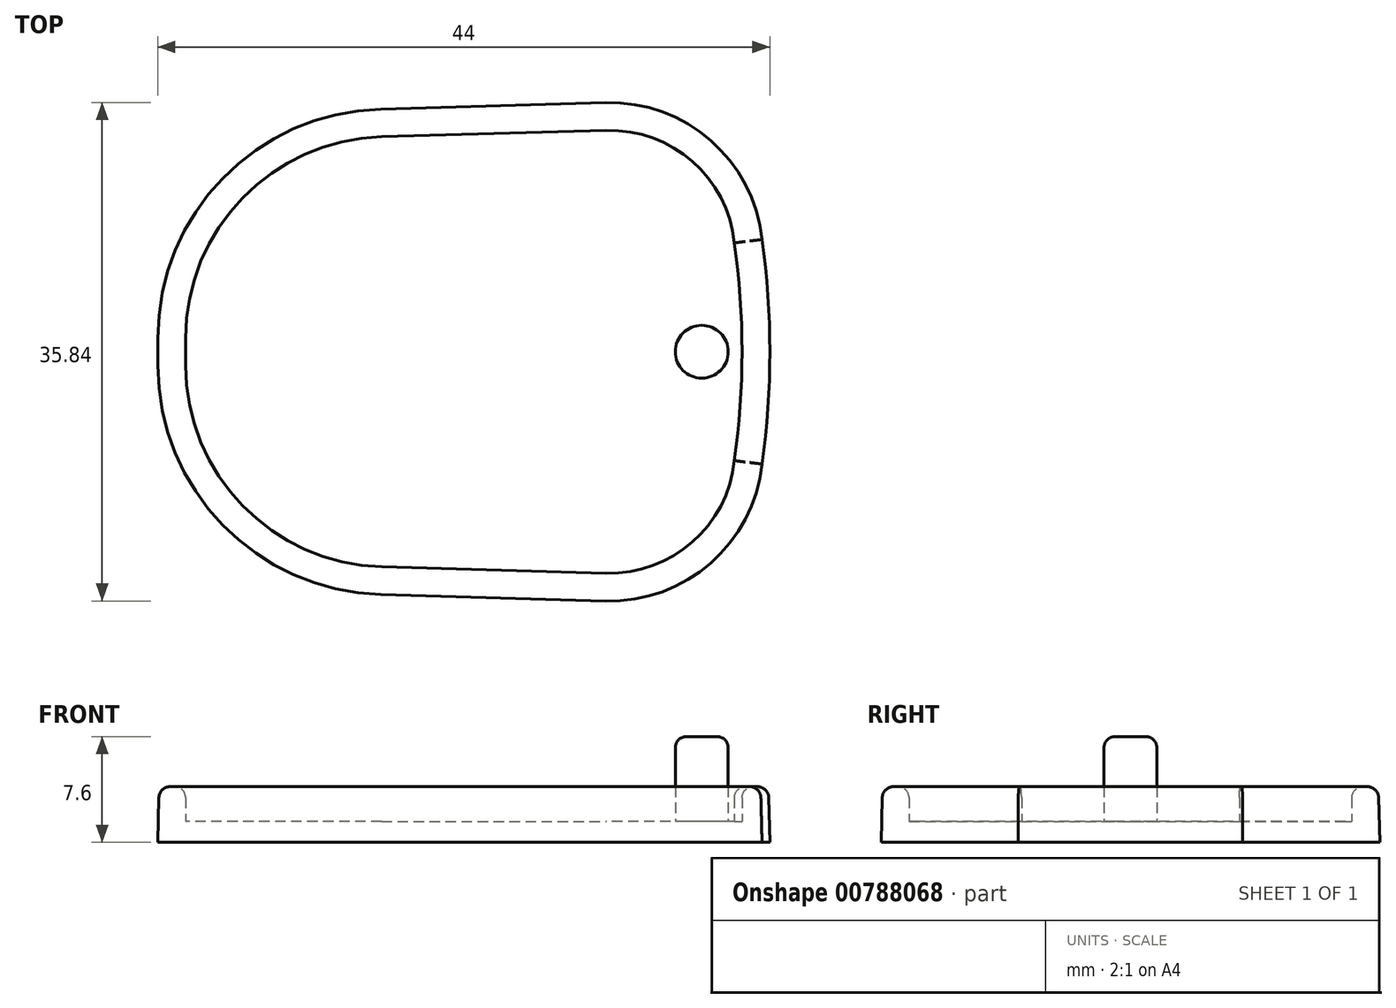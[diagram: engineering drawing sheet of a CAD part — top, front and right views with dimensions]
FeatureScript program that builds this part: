
annotation { "Feature Type Name" : "Feature", "Feature Type Description" : "" }
export const myFeature = defineFeature(function(context is Context, id is Id, definition is map)
    precondition{}
    {
        {
            var Q0;
            Q0=qCreatedBy(makeId("Top.planeOp"),FACE);
            var sketch = newSketch(context, id + "F0", { "sketchPlane" : qUnion([Q0])});
            skLineSegment(sketch, "E0", {"start": v(-22, 17) * mm, "end": v(22, 18.25) * mm, "construction": true});
            skLineSegment(sketch, "E1", {"start": v(22, 18.25) * mm, "end": v(22, -18.25) * mm, "construction": true});
            skLineSegment(sketch, "E2", {"start": v(22, -18.25) * mm, "end": v(-22, -17) * mm, "construction": true});
            skLineSegment(sketch, "E3", {"start": v(-22, -17) * mm, "end": v(-22, 17) * mm, "construction": true});
            skPoint(sketch, "E4", {"position": v(-22, 0) * mm});
            skPoint(sketch, "E5", {"position": v(22, 0) * mm});
            skPoint(sketch, "E6", {"position": v(0, 17.63) * mm});
            skArc(sketch, "E7", {"start": v(-5.97, 17.46) * mm, "mid": v(-17.33, 12.46) * mm, "end": v(-22, 0.96) * mm});
            skLineSegment(sketch, "E8", {"start": v(-22, 0) * mm, "end": v(-22, 0.96) * mm});
            skArc(sketch, "E9", {"start": v(22, 0) * mm, "mid": v(21.86, 4.05) * mm, "end": v(21.44, 8.07) * mm});
            skArc(sketch, "E10", {"start": v(21.44, 8.07) * mm, "mid": v(17.74, 15.2) * mm, "end": v(10.18, 17.91) * mm});
            skLineSegment(sketch, "E11", {"start": v(-36, 0) * mm, "end": v(21.44, 8.07) * mm, "construction": true});
            skLineSegment(sketch, "E12", {"start": v(-12.73, 0) * mm, "end": v(12.59, 0) * mm, "construction": true});
            skLineSegment(sketch, "E13.MirrorCS", {"start": v(-22, 0) * mm, "end": v(-22, -0.96) * mm});
            skArc(sketch, "E14.MirrorCS", {"start": v(-5.97, -17.46) * mm, "mid": v(-17.33, -12.46) * mm, "end": v(-22, -0.96) * mm});
            skPoint(sketch, "E15.MirrorP", {"position": v(0, -17.63) * mm});
            skArc(sketch, "E16.MirrorCS", {"start": v(21.44, -8.07) * mm, "mid": v(17.74, -15.2) * mm, "end": v(10.18, -17.91) * mm});
            skArc(sketch, "E17.MirrorCS", {"start": v(22, 0) * mm, "mid": v(21.86, -4.05) * mm, "end": v(21.44, -8.07) * mm});
            skLineSegment(sketch, "E18", {"start": v(-5.97, 17.46) * mm, "end": v(10.18, 17.91) * mm});
            skLineSegment(sketch, "E19", {"start": v(-5.97, -17.46) * mm, "end": v(10.18, -17.91) * mm});
            skCircle(sketch, "E20", {"center": v(17.1, 0) * mm, "radius": 1.9 * mm});
            skLineSegment(sketch, "E21.0", {"start": v(-5.91, 15.46) * mm, "end": v(10.24, 15.92) * mm});
            skArc(sketch, "E21.1", {"start": v(19.45, 7.83) * mm, "mid": v(16.43, 13.68) * mm, "end": v(10.24, 15.92) * mm});
            skArc(sketch, "E21.2", {"start": v(-5.91, 15.46) * mm, "mid": v(-15.9, 11.07) * mm, "end": v(-20, 0.96) * mm});
            skArc(sketch, "E21.3", {"start": v(20, 0) * mm, "mid": v(19.86, 3.92) * mm, "end": v(19.45, 7.83) * mm});
            skArc(sketch, "E21.4", {"start": v(20, 0) * mm, "mid": v(19.86, -3.92) * mm, "end": v(19.45, -7.83) * mm});
            skArc(sketch, "E21.5", {"start": v(19.45, -7.83) * mm, "mid": v(16.43, -13.68) * mm, "end": v(10.24, -15.92) * mm});
            skLineSegment(sketch, "E21.6", {"start": v(-20, 0) * mm, "end": v(-20, 0.96) * mm});
            skLineSegment(sketch, "E21.7", {"start": v(-20, 0) * mm, "end": v(-20, -0.96) * mm});
            skArc(sketch, "E21.8", {"start": v(-5.91, -15.46) * mm, "mid": v(-15.9, -11.07) * mm, "end": v(-20, -0.96) * mm});
            skLineSegment(sketch, "E21.9", {"start": v(-5.91, -15.46) * mm, "end": v(10.24, -15.92) * mm});
            skSolve(sketch);
        }
        {
            var Q0;
            Q0=makeQuery(id+"F0.imprint","IMPRINT",FACE,{"disambiguationData":[TD([[makeQuery(id+"F0.imprint","IMPRINT",EDGE,{"derivedFrom":sQuery(id+"F0.wireOp",EDGE,"E7")}),1.0]])]});
            extrude(context, id + "F1", {"entities" : qUnion([Q0]), "depth" : 4 * mm, "offsetDistance" : 25 * mm});
        }
        {
            var Q0;
            Q0=makeQuery(id+"F0.imprint","IMPRINT",FACE,{"disambiguationData":[TD([[makeQuery(id+"F0.imprint","IMPRINT",EDGE,{"derivedFrom":sQuery(id+"F0.wireOp",EDGE,"E20")}),1.0]])]});
            extrude(context, id + "F2", {"entities" : qUnion([Q0]), "operationType" : NewBodyOperationType.ADD, "depth" : 7.6 * mm, "offsetDistance" : 25 * mm});
        }
        {
            var Q0;
            Q0=makeQuery(id+"F0.imprint","IMPRINT",FACE,{"disambiguationData":[TD([[makeQuery(id+"F0.imprint","IMPRINT",EDGE,{"derivedFrom":sQuery(id+"F0.wireOp",EDGE,"E20")}),-1.0]])]});
            extrude(context, id + "F3", {"entities" : qUnion([Q0]), "operationType" : NewBodyOperationType.ADD, "depth" : 1.5 * mm, "offsetDistance" : 25 * mm});
        }
        {
            var Q0;
            Q0=makeQuery(id+"F1.opExtrude","CAP_EDGE",EDGE,{"disambiguationData":[OSD([sQuery(id+"F0.wireOp",EDGE,"E19")])],"isStart":false});
            chamfer(context, id + "F4", {"entities" : qUnion([Q0]), "chamferType" : ChamferType.TWO_OFFSETS, "width1" : 0.1 * mm, "oppositeDirection" : false, "width2" : 4 * mm, "tangentPropagation" : true});
        }
        {
            var Q0;
            {var subQ0=sQuery(id+"F0.wireOp",EDGE,"E18");Q0=makeQuery(id+"F4.opChamfer","BLEND_EDGE",EDGE,{"blendedFrom":[makeQuery(id+"F1.opExtrude","CAP_EDGE",EDGE,{"disambiguationData":[OSD([subQ0])],"isStart":false}),makeQuery(id+"F1.opExtrude","CAP_FACE",FACE,{"disambiguationData":[OSD([sQuery(id+"F0.wireOp",EDGE,"E7"),sQuery(id+"F0.wireOp",EDGE,"E8"),sQuery(id+"F0.wireOp",EDGE,"E9"),sQuery(id+"F0.wireOp",EDGE,"E10"),sQuery(id+"F0.wireOp",EDGE,"E13.MirrorCS"),sQuery(id+"F0.wireOp",EDGE,"E14.MirrorCS"),sQuery(id+"F0.wireOp",EDGE,"E16.MirrorCS"),sQuery(id+"F0.wireOp",EDGE,"E17.MirrorCS"),subQ0,sQuery(id+"F0.wireOp",EDGE,"E19"),sQuery(id+"F0.wireOp",EDGE,"E21.0"),sQuery(id+"F0.wireOp",EDGE,"E21.1"),sQuery(id+"F0.wireOp",EDGE,"E21.2"),sQuery(id+"F0.wireOp",EDGE,"E21.3"),sQuery(id+"F0.wireOp",EDGE,"E21.4"),sQuery(id+"F0.wireOp",EDGE,"E21.5"),sQuery(id+"F0.wireOp",EDGE,"E21.6"),sQuery(id+"F0.wireOp",EDGE,"E21.7"),sQuery(id+"F0.wireOp",EDGE,"E21.8"),sQuery(id+"F0.wireOp",EDGE,"E21.9")])],"isStart":false})],"blendedInto":[makeQuery(id+"F1.opExtrude","CAP_FACE",FACE,{"disambiguationData":[OSD([sQuery(id+"F0.wireOp",EDGE,"E7"),sQuery(id+"F0.wireOp",EDGE,"E8"),sQuery(id+"F0.wireOp",EDGE,"E9"),sQuery(id+"F0.wireOp",EDGE,"E10"),sQuery(id+"F0.wireOp",EDGE,"E13.MirrorCS"),sQuery(id+"F0.wireOp",EDGE,"E14.MirrorCS"),sQuery(id+"F0.wireOp",EDGE,"E16.MirrorCS"),sQuery(id+"F0.wireOp",EDGE,"E17.MirrorCS"),subQ0,sQuery(id+"F0.wireOp",EDGE,"E19"),sQuery(id+"F0.wireOp",EDGE,"E21.0"),sQuery(id+"F0.wireOp",EDGE,"E21.1"),sQuery(id+"F0.wireOp",EDGE,"E21.2"),sQuery(id+"F0.wireOp",EDGE,"E21.3"),sQuery(id+"F0.wireOp",EDGE,"E21.4"),sQuery(id+"F0.wireOp",EDGE,"E21.5"),sQuery(id+"F0.wireOp",EDGE,"E21.6"),sQuery(id+"F0.wireOp",EDGE,"E21.7"),sQuery(id+"F0.wireOp",EDGE,"E21.8"),sQuery(id+"F0.wireOp",EDGE,"E21.9")])],"isStart":false})]});}
            var Q1;
            Q1=makeQuery(id+"F1.opExtrude","CAP_EDGE",EDGE,{"disambiguationData":[OSD([sQuery(id+"F0.wireOp",EDGE,"E21.0")])],"isStart":false});
            var Q2;
            Q2=makeQuery(id+"F1.opExtrude","CAP_EDGE",EDGE,{"disambiguationData":[OSD([sQuery(id+"F0.wireOp",EDGE,"E21.3"),sQuery(id+"F0.wireOp",EDGE,"E21.4")])],"isStart":false});
            var Q3;
            Q3=makeQuery(id+"F3.opExtrude","CAP_EDGE",EDGE,{"disambiguationData":[OSD([sQuery(id+"F0.wireOp",EDGE,"E20")])],"isStart":false});
            var Q4;
            Q4=makeQuery(id+"F2.opExtrude","CAP_EDGE",EDGE,{"disambiguationData":[OSD([sQuery(id+"F0.wireOp",EDGE,"E20")])],"isStart":false});
            fillet(context, id + "F5", {"entities" : qUnion([Q0, Q1, Q2, Q3, Q4]), "radius" : 0.8 * mm, "tangentPropagation" : true, "allowEdgeOverflow" : false});
        }
    });
